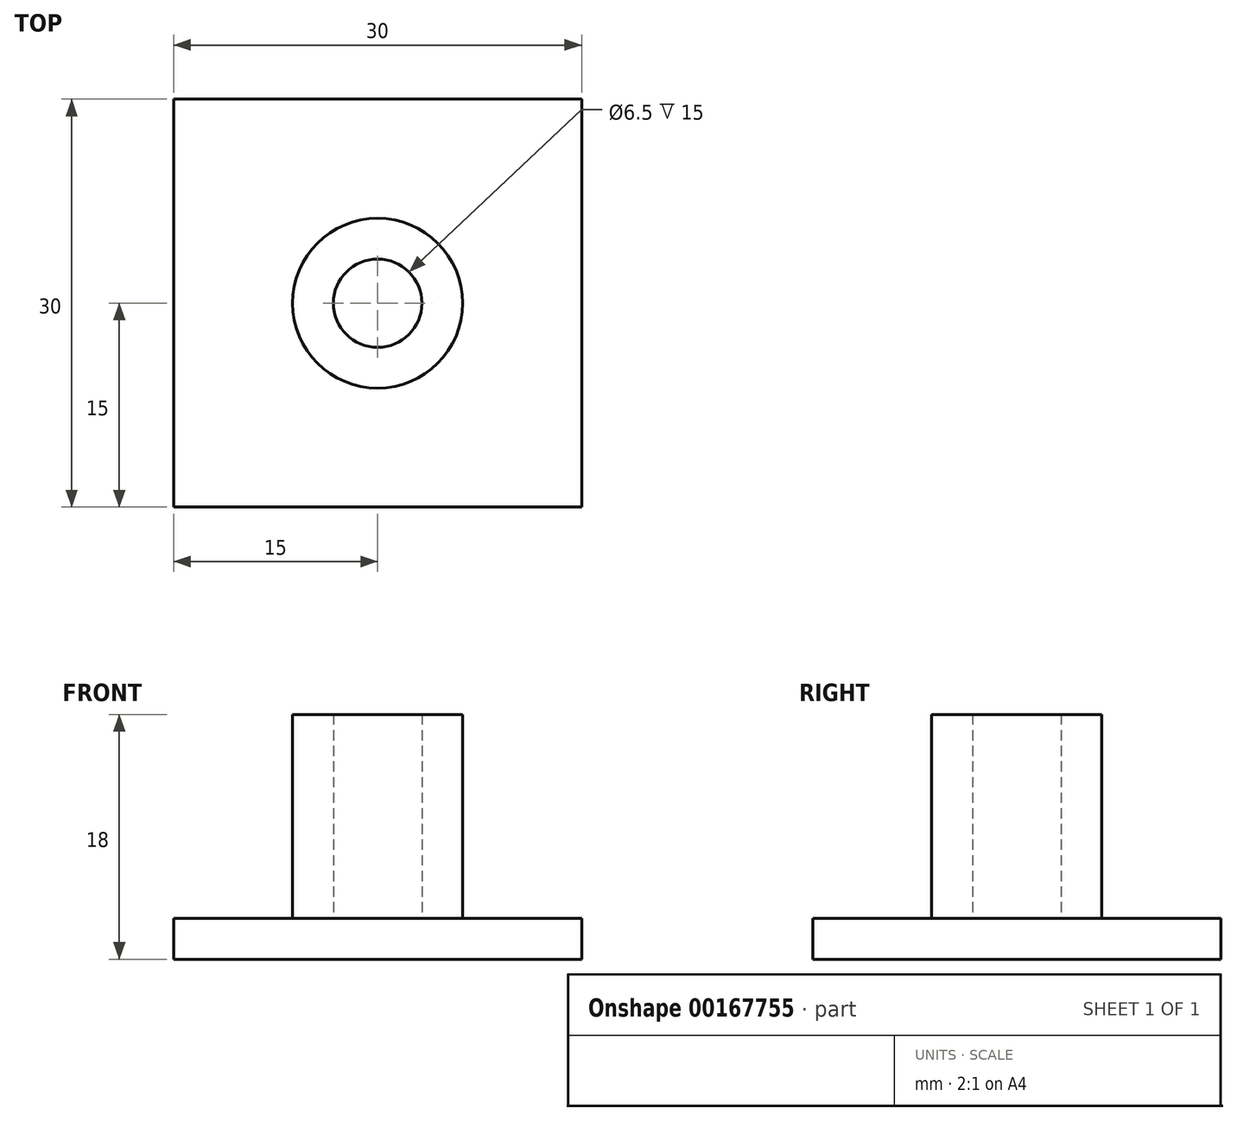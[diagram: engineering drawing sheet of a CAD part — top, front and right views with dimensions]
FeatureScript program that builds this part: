
annotation { "Feature Type Name" : "Feature", "Feature Type Description" : "" }
export const myFeature = defineFeature(function(context is Context, id is Id, definition is map)
    precondition{}
    {
        {
            var Q0;
            Q0=qCreatedBy(makeId("Top.planeOp"),FACE);
            var sketch = newSketch(context, id + "F0", { "sketchPlane" : qUnion([Q0]) });
            skLineSegment(sketch, "E0.bottom", {"start": v(-15, 15) * mm, "end": v(15, 15) * mm});
            skLineSegment(sketch, "E0.top", {"start": v(-15, -15) * mm, "end": v(15, -15) * mm});
            skLineSegment(sketch, "E0.left", {"start": v(-15, 15) * mm, "end": v(-15, -15) * mm});
            skLineSegment(sketch, "E0.right", {"start": v(15, 15) * mm, "end": v(15, -15) * mm});
            skLineSegment(sketch, "E1", {"start": v(-15, 15) * mm, "end": v(15, -15) * mm, "construction": true});
            skSolve(sketch);
        }
        {
            var Q0;
            Q0 = qSketchRegion(id + "F0", true);
            extrude(context, id + "F1", {"entities" : qUnion([Q0]), "depth" : 3 * mm, "offsetDistance" : 25 * mm});
        }
        {
            var Q0;
            Q0=makeQuery(id+"F1.opExtrude","CAP_FACE",FACE,{"disambiguationData":[OSD([sQuery(id+"F0.wireOp",EDGE,"E0.bottom"),sQuery(id+"F0.wireOp",EDGE,"E0.top"),sQuery(id+"F0.wireOp",EDGE,"E0.left"),sQuery(id+"F0.wireOp",EDGE,"E0.right")])],"isStart":false});
            var sketch = newSketch(context, id + "F2", { "sketchPlane" : qUnion([Q0]) });
            skCircle(sketch, "E2", {"center": v(0, 0) * mm, "radius": 6.25 * mm});
            skCircle(sketch, "E3", {"center": v(0, 0) * mm, "radius": 3.25 * mm});
            skSolve(sketch);
        }
        {
            var Q0;
            Q0 = qSketchRegion(id + "F2", true);
            extrude(context, id + "F3", {"entities" : qUnion([Q0]), "operationType" : NewBodyOperationType.ADD, "depth" : 15 * mm, "offsetDistance" : 25 * mm});
        }
    });
